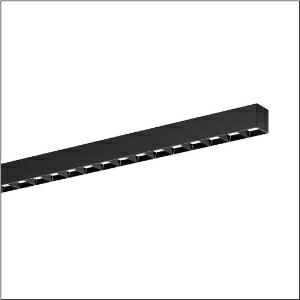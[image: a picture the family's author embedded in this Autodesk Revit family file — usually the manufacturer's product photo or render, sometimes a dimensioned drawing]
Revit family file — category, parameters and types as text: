
# Revit family: silica_r__21_51mx24tat4b_951d
name_source: partatom
category: Lighting Fixtures
units: mm (PartAtom-declared; Revit-internal decimal feet)

## family parameters
Cut with Voids When Loaded = No
Host = Face
Light Source = No
Part Type = Normal
Room Calculation Point = No
Round Connector Dimension = Use Diameter
Shared = No

## types (1)
- --- (1 x LED, 3280 lm, 32.4 W, 6500K)
    Apparent Load = 32 VA
    CIE Flux Codes = 74 94 99 100 100
    Color Rendering = 80
    Color Temperature = 6500K
    Default Elevation = 1800 mm
    Description = Silica® 21, office luminaire, primary light control with darklight reflector, of PMMA, black, light emission: direct distribution, primary light characteristic: asymmetric, installation type: surface-mounted, LED, rated luminous flux: 3.280lm, luminous efficacy: 96lm/W, light colour: 8tw, colour temperature: 2700..6500K, control gear: ECG DALI, with terminal, 3+2-pole, max. 2.5mm², mains connection: 220..240V, AC, 50/60Hz, rated input power: 34.1W, luminaire housing, of aluminium, jet black (RAL 9005), length: 1.204mm, width: 53mm, height: 53mm, protection rating (complete): IP20, insulation class (complete): insulation class I (protective earthing), certification: CE, permissible operating ambient temperature: 0..+35°C, standard: EN 50419, packaging unit: 1 piece
    Height = 0 mm  [stored 0 ft]
    Lamp = 1 x LED
    Lamp Light Flux = 3280 lm
    Lamp Power = 32.4 W
    Lamp count = 1
    Length = 1204 mm
    Luminous efficacy = 101 lm/W
    Manufacturer = Siteco
    ModVariant = No
    Model = 51MX24TAT4B
    Mounting Place = Ceiling
    Mounting Type = Recessed
    Number of Poles = 1
    OnlyDefault = Yes
    Power Factor = 1
    Product Name = Silica® 21
    Product group = office luminaire | ceiling recessed
    ProductGroupID = 401
    Protection Class = Protection class I
    Protection Degree = IP 20
    RLX_Detail_Level = 1
    RLX_Emergency_Light_Flux = 0 lm
    RLX_Emergency_Type = 0
    RLX_Emergency_Type_DB = No
    RlxData = <blob elided: 40609 chars, md5=b2a038d7>
    Socket = socket
    Standby Power = 0 W
    System Light Flux = 3280 lm
    System Power = 32 W
    Type Comments = individual setting
    Type Image = l_1313577.jpg
    URL = http://relux.com
    VarID = @adj_089367
    Voltage = 0 V
    Weight = 0.00 kg
    Width = 53 mm

note: [stored X ft] marks values corroborated as IEEE doubles in the binary element streams (Revit-internal decimal feet)

## geometry (parser evidence)
native form markers: Blend x4, Sweep x10
no freeform markers — native parametric forms only
